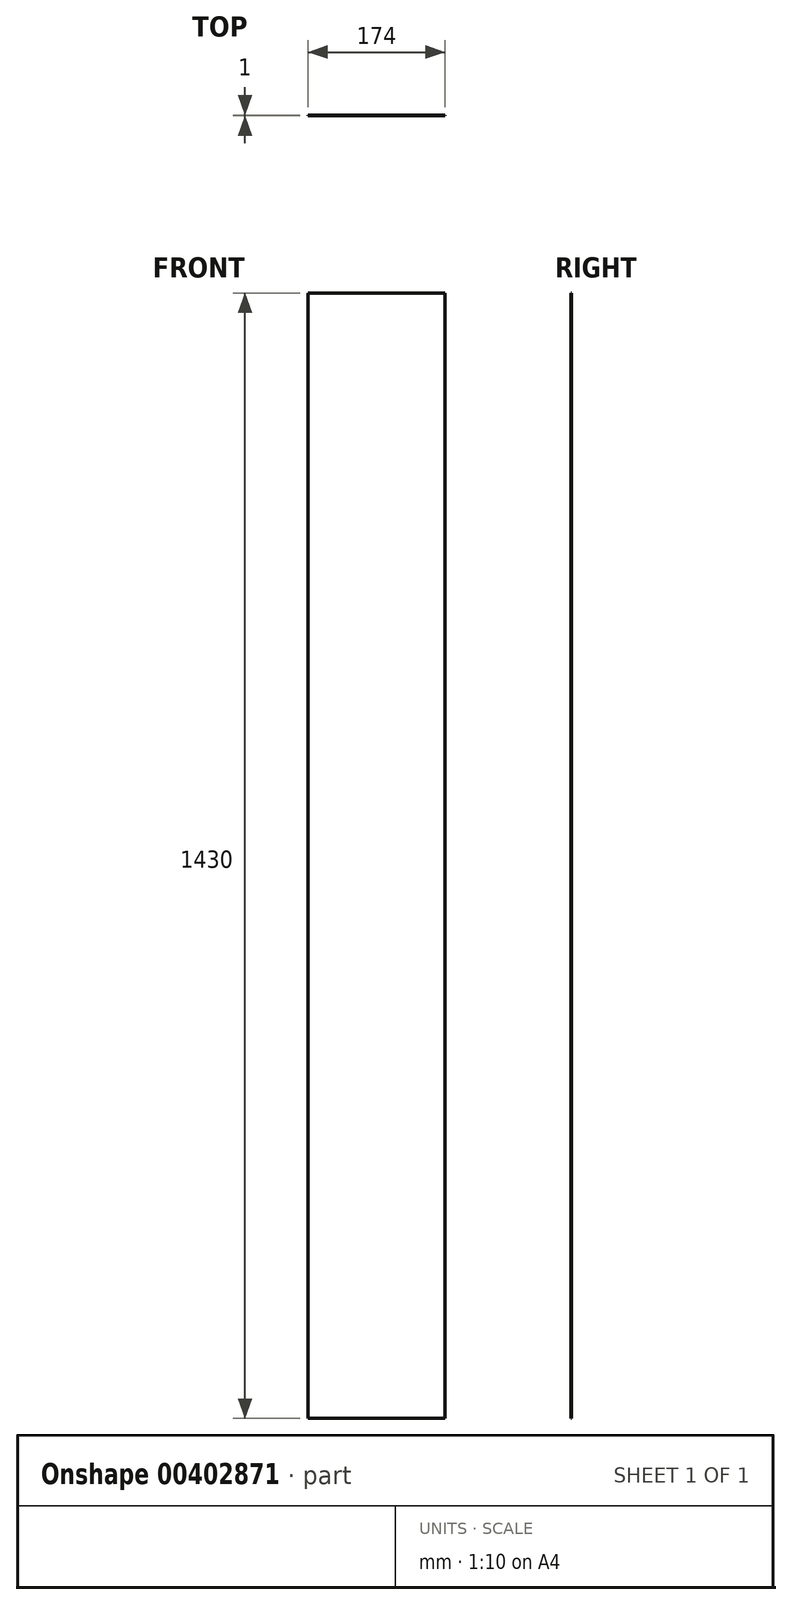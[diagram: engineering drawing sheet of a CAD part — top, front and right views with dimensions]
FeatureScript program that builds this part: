
annotation { "Feature Type Name" : "Feature", "Feature Type Description" : "" }
export const myFeature = defineFeature(function(context is Context, id is Id, definition is map)
    precondition{}
    {
        {
            var Q0;
            Q0=qCreatedBy(makeId("Front.planeOp"),FACE);
            var sketch = newSketch(context, id + "F0", { "sketchPlane" : qUnion([Q0])});
            skLineSegment(sketch, "E0.bottom", {"start": v(-87, 715) * mm, "end": v(87, 715) * mm});
            skLineSegment(sketch, "E0.top", {"start": v(-87, -715) * mm, "end": v(87, -715) * mm});
            skLineSegment(sketch, "E0.left", {"start": v(-87, 715) * mm, "end": v(-87, -715) * mm});
            skLineSegment(sketch, "E0.right", {"start": v(87, 715) * mm, "end": v(87, -715) * mm});
            skPoint(sketch, "E0.middle", {"position": v(0, 0) * mm});
            skSolve(sketch);
        }
        {
            var Q0;
            Q0=makeQuery(id+"F0.imprint","IMPRINT",FACE,{"disambiguationData":[TD([[makeQuery(id+"F0.imprint","IMPRINT",EDGE,{"derivedFrom":sQuery(id+"F0.wireOp",EDGE,"E0.bottom")}),-1.0]])]});
            extrude(context, id + "F1", {"entities" : qUnion([Q0]), "depth" : 1 * mm});
        }
    });
